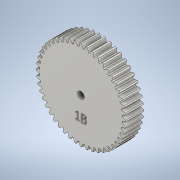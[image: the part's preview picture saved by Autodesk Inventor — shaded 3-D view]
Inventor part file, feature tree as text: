
AUTODESK INVENTOR PART (.ipt)
format: ipt  version: 2021 (Build 250183000, 183)  size: 408,576 bytes
history: native  units: mm (DEFAULTED — no unit token found)
features: sketch x4, plane x3, other x3, extrude x1, hole x1, emboss x1
ambient origin geometry x8: Origin, YZ Plane, XZ Plane, XY Plane, X Axis, Y Axis, Z Axis, Center Point
bodies: Solid1 (feature_tree)
feature tree (13):
  extrude  "Extrusion1"  Depth=8.0mm TaperAngle=0.0deg
  plane  "Work Plane2"
  plane  "Work Plane8"
  plane  "Work Plane9"
  other  "Spur Gear"
  hole  "Hole1"  [1 undecoded]
  emboss  "Emboss1"
  sketch  "Sketch1"  dims[d0=39.68mm d1=8.0mm d2=0.0mm]
  sketch  "Sketch2"  dims[d3=38.4mm d4=10.0mm d5=0.0mm]
  other  "Srf1"
  sketch  "Sketch3"  dims[d16=28.8mm]
  sketch  "Sketch4"  dims[d17=0.0mm d34=0.654498mm d39=0.0mm d41=0.0mm d43=28.8mm d46=28.8mm d47=0.0mm d48=0.0mm d49=3.0mm d50=3.0mm d51=6.0mm d52=4.0mm d53=2.0mm d54=90.0deg d55=8.0mm d56=20.594885mm d57=1.0mm d58=0.0mm]
  other  "Pitch Diameter"
note: 1 required parameter value undecoded (feature->parameter linkage not recoverable at this tier; creation-order binding heuristic only, values carry confidence <= 0.55)
